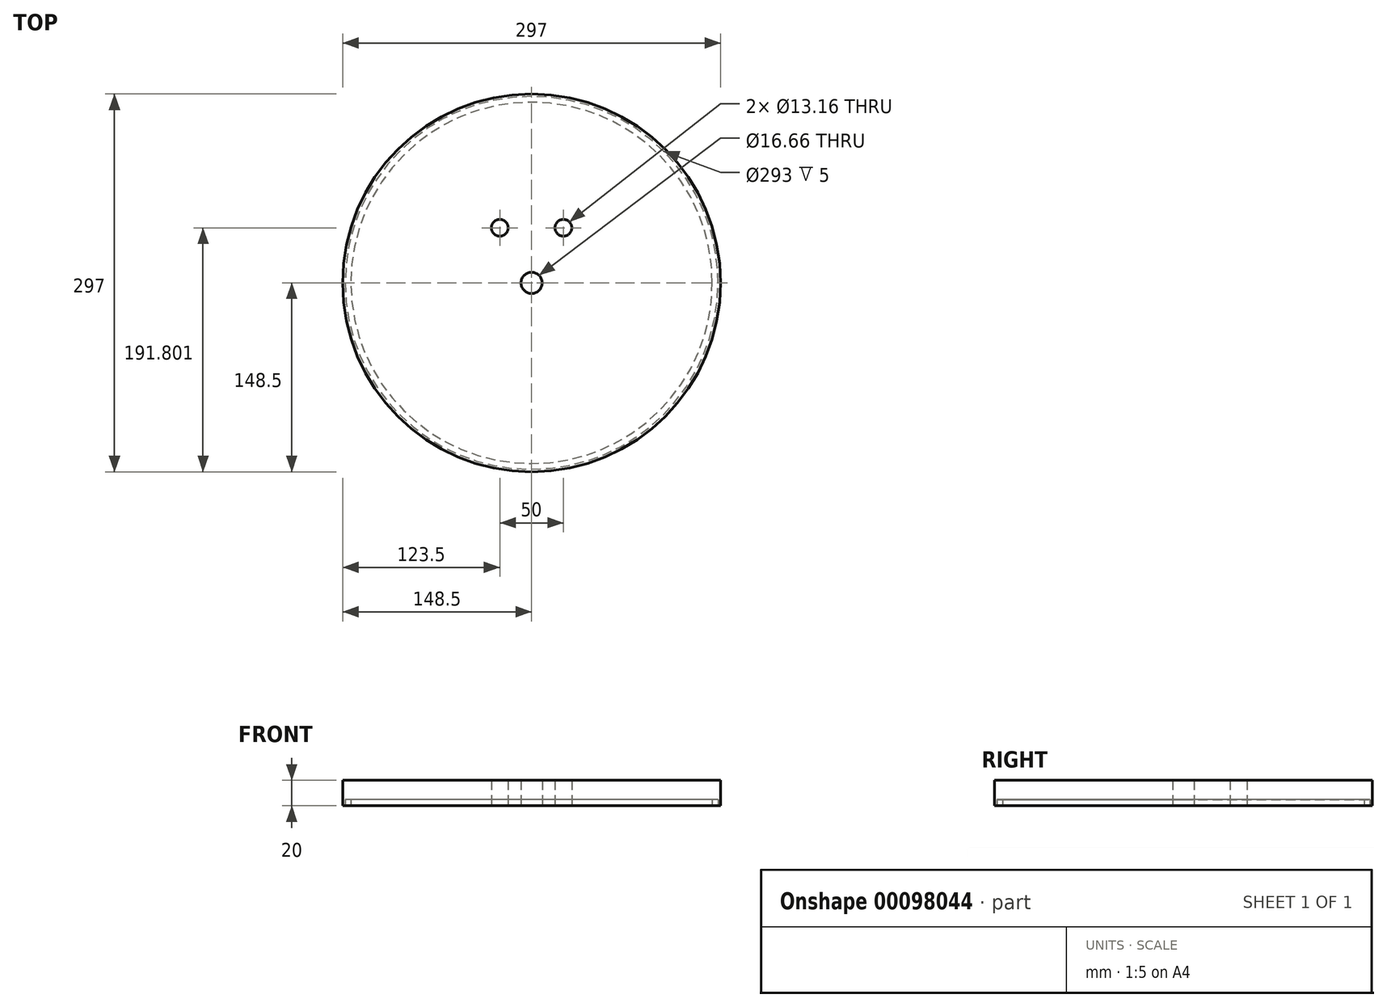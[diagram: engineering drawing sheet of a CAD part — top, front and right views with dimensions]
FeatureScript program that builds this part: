
annotation { "Feature Type Name" : "Feature", "Feature Type Description" : "" }
export const myFeature = defineFeature(function(context is Context, id is Id, definition is map)
    precondition{}
    {
        {
            var Q0;
            Q0=qCreatedBy(makeId("Top.planeOp"),FACE);
            var sketch = newSketch(context, id + "F0", { "sketchPlane" : qUnion([Q0])});
            skCircle(sketch, "E0", {"center": v(0, 0) * mm, "radius": 148.5 * mm});
            skCircle(sketch, "E1", {"center": v(0, 0) * mm, "radius": 8.33 * mm});
            skCircle(sketch, "E2", {"center": v(-25, 43.3) * mm, "radius": 6.58 * mm});
            skCircle(sketch, "E3", {"center": v(25, 43.3) * mm, "radius": 6.58 * mm});
            skLineSegment(sketch, "E4", {"start": v(-25, 43.3) * mm, "end": v(25, 43.3) * mm, "construction": true});
            skLineSegment(sketch, "E5", {"start": v(25, 43.3) * mm, "end": v(0, 0) * mm, "construction": true});
            skLineSegment(sketch, "E6", {"start": v(0, 0) * mm, "end": v(-25, 43.3) * mm, "construction": true});
            skLineSegment(sketch, "E7", {"start": v(0, 0) * mm, "end": v(0, 43.3) * mm, "construction": true});
            skSolve(sketch);
        }
        {
            var Q0;
            Q0=makeQuery(id+"F0.imprint","IMPRINT",FACE,{"disambiguationData":[TD([[makeQuery(id+"F0.imprint","IMPRINT",EDGE,{"derivedFrom":sQuery(id+"F0.wireOp",EDGE,"E0")}),1.0]])]});
            var Q1;
            Q1=makeQuery(id+"F0.imprint","IMPRINT",FACE,{"disambiguationData":[TD([[makeQuery(id+"F0.imprint","IMPRINT",EDGE,{"derivedFrom":sQuery(id+"F0.wireOp",EDGE,"LIXrByum-44Gz-KbWN-PE50-DMeDG7NppI0J")}),1.0]])]});
            var Q2;
            Q2=makeQuery(id+"F0.imprint","IMPRINT",FACE,{"disambiguationData":[TD([[makeQuery(id+"F0.imprint","IMPRINT",EDGE,{"derivedFrom":sQuery(id+"F0.wireOp",EDGE,"oq2Y4278-V4UZ-WgQw-2GIa-DsGsglEtdsp5")}),1.0]])]});
            extrude(context, id + "F1", {"entities" : qUnion([Q0, Q1, Q2]), "depth" : 20 * mm});
        }
        {
            var Q0;
            Q0=makeQuery(id+"F0.imprint","IMPRINT",FACE,{"disambiguationData":[TD([[makeQuery(id+"F0.imprint","IMPRINT",EDGE,{"derivedFrom":sQuery(id+"F0.wireOp",EDGE,"E0")}),1.0]])]});
            var sketch = newSketch(context, id + "F2", { "sketchPlane" : qUnion([Q0])});
            skCircle(sketch, "E8", {"center": v(0, 0) * mm, "radius": 146.5 * mm});
            skCircle(sketch, "E9", {"center": v(0, 0) * mm, "radius": 142 * mm});
            skSolve(sketch);
        }
        {
            var Q0;
            Q0=qSketchRegion(id+"F2",true);
            extrude(context, id + "F3", {"entities" : qUnion([Q0]), "operationType" : NewBodyOperationType.REMOVE, "depth" : 5 * mm});
        }
    });
